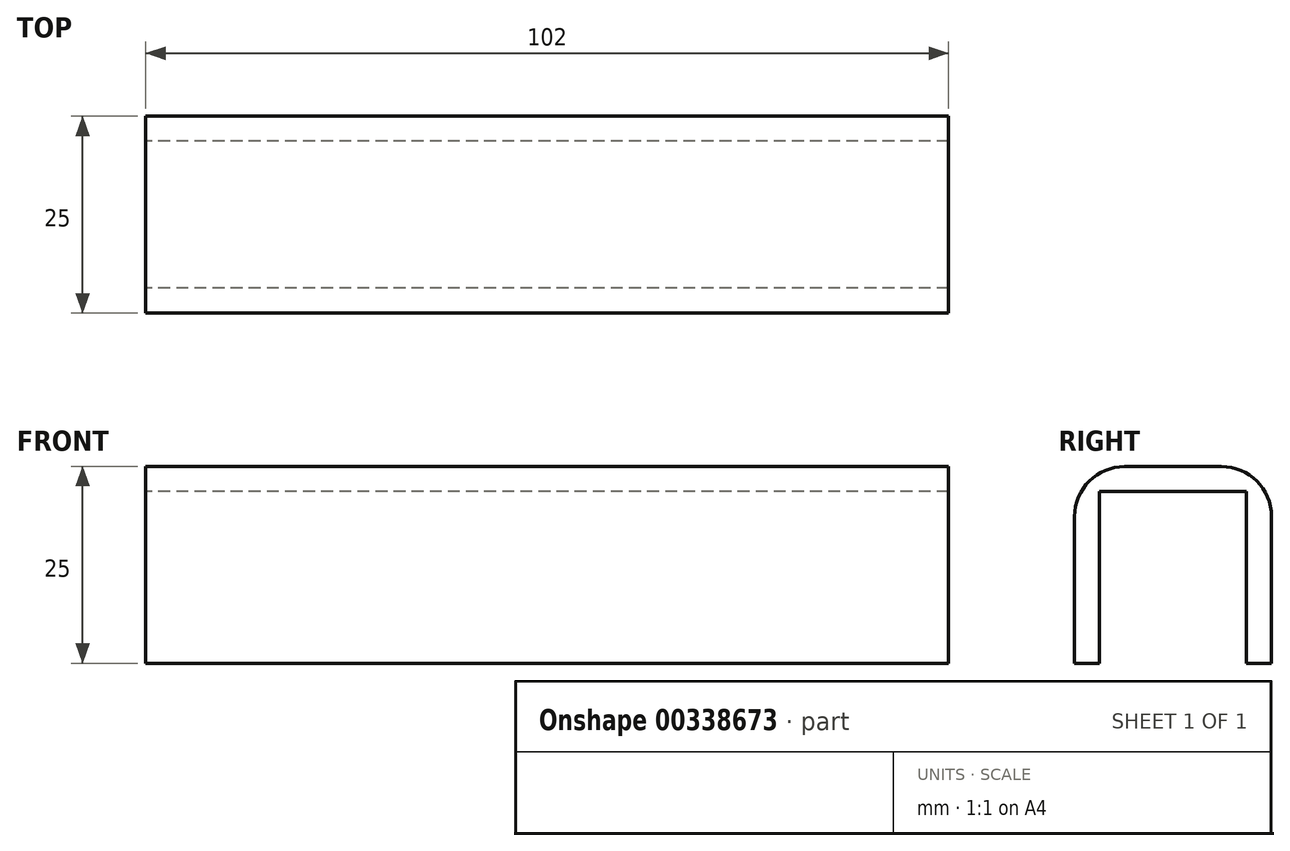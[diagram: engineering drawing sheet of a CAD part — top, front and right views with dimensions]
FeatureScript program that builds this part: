
annotation { "Feature Type Name" : "Feature", "Feature Type Description" : "" }
export const myFeature = defineFeature(function(context is Context, id is Id, definition is map)
    precondition{}
    {
        {
            var Q0;
            Q0=qCreatedBy(makeId("Right.planeOp"),FACE);
            var sketch = newSketch(context, id + "F0", { "sketchPlane" : qUnion([Q0])});
            skLineSegment(sketch, "E0", {"start": v(0, 0) * mm, "end": v(0, 25) * mm});
            skLineSegment(sketch, "E1", {"start": v(0, 25) * mm, "end": v(25, 25) * mm});
            skLineSegment(sketch, "E2", {"start": v(25, 25) * mm, "end": v(25, 0) * mm});
            skLineSegment(sketch, "E3.0", {"start": v(21.83, 21.83) * mm, "end": v(21.83, 0) * mm});
            skLineSegment(sketch, "E3.1", {"start": v(3.17, 21.83) * mm, "end": v(21.83, 21.83) * mm});
            skLineSegment(sketch, "E3.2", {"start": v(3.17, 0) * mm, "end": v(3.17, 21.83) * mm});
            skLineSegment(sketch, "E4", {"start": v(0, 0) * mm, "end": v(3.17, 0) * mm});
            skLineSegment(sketch, "E5", {"start": v(21.83, 0) * mm, "end": v(25, 0) * mm});
            skSolve(sketch);
        }
        {
            var Q0;
            Q0=makeQuery(id+"F0.imprint","IMPRINT",FACE,{"disambiguationData":[TD([[makeQuery(id+"F0.imprint","IMPRINT",EDGE,{"derivedFrom":sQuery(id+"F0.wireOp",EDGE,"E0")}),-1.0]])]});
            extrude(context, id + "F1", {"entities" : qUnion([Q0]), "endBound" : BoundingType.SYMMETRIC, "depth" : 102 * mm});
        }
        {
            var Q0;
            Q0=makeQuery(id+"F1.opExtrude","SWEPT_EDGE",EDGE,{"disambiguationData":[OSD([sQuery(id+"F0.wireOp",EDGE,"E1"),sQuery(id+"F0.wireOp",EDGE,"E2")])]});
            var Q1;
            Q1=makeQuery(id+"F1.opExtrude","SWEPT_EDGE",EDGE,{"disambiguationData":[OSD([sQuery(id+"F0.wireOp",EDGE,"E0"),sQuery(id+"F0.wireOp",EDGE,"E1")])]});
            fillet(context, id + "F2", {"entities" : qUnion([Q0, Q1]), "radius" : 6.35 * mm, "tangentPropagation" : true, "allowEdgeOverflow" : false});
        }
    });
